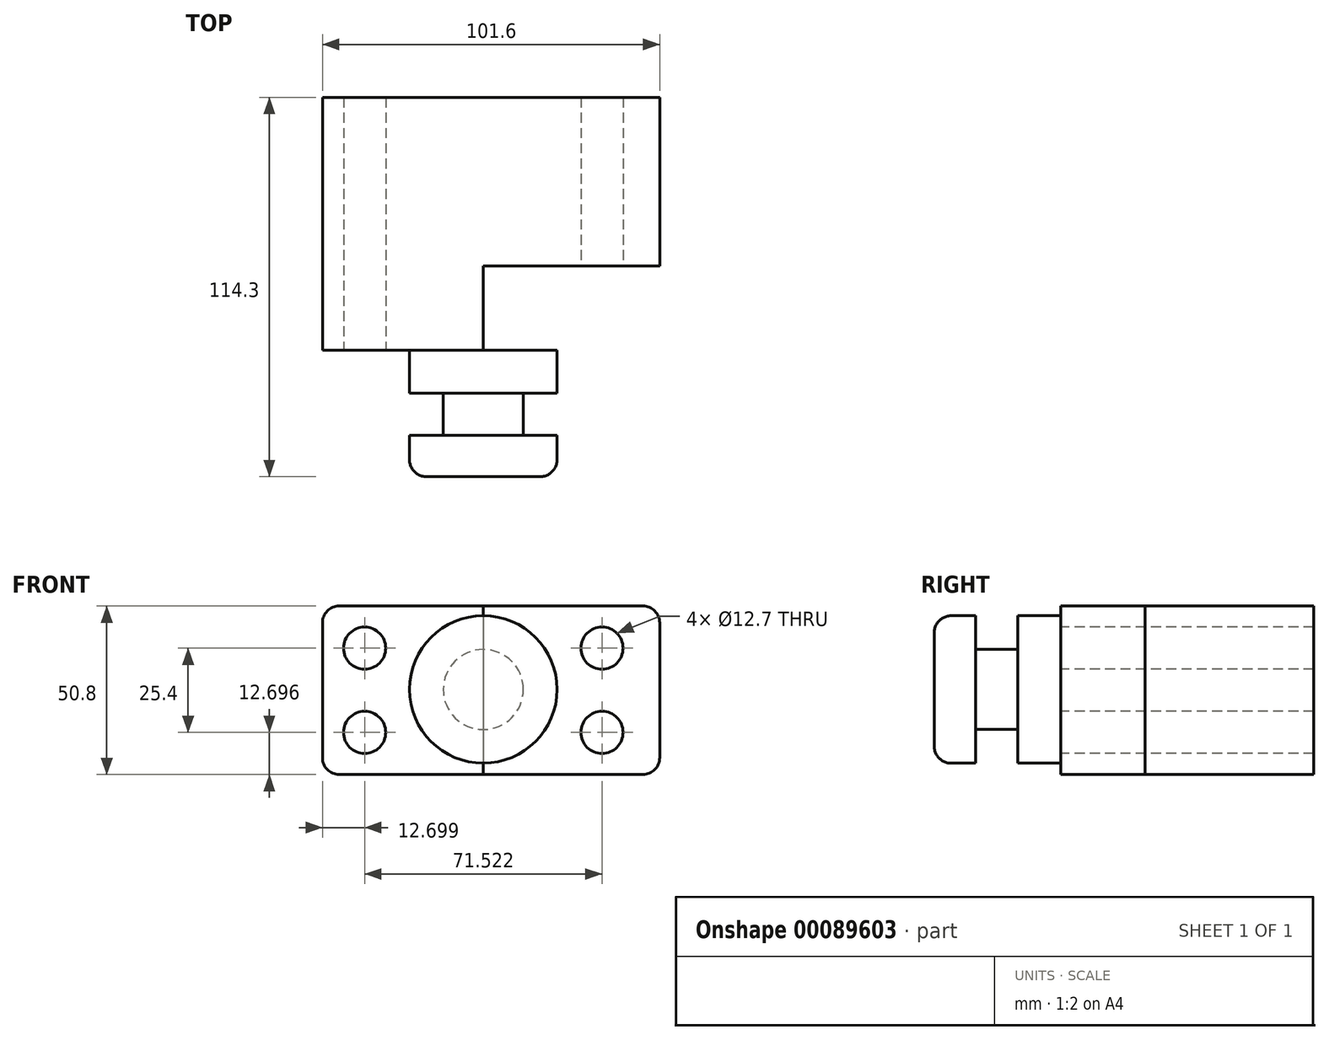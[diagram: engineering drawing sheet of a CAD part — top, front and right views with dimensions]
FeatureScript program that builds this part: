
annotation { "Feature Type Name" : "Feature", "Feature Type Description" : "" }
export const myFeature = defineFeature(function(context is Context, id is Id, definition is map)
    precondition{}
    {
        {
            var Q0;
            Q0=qCreatedBy(makeId("Front.planeOp"),FACE);
            var sketch = newSketch(context, id + "F0", { "sketchPlane" : qUnion([Q0])});
            skLineSegment(sketch, "E0", {"start": v(-48.46, 25.17) * mm, "end": v(53.14, 25.17) * mm});
            skLineSegment(sketch, "E1", {"start": v(53.14, 25.17) * mm, "end": v(53.14, -25.63) * mm});
            skLineSegment(sketch, "E2", {"start": v(53.14, -25.63) * mm, "end": v(-48.46, -25.63) * mm});
            skLineSegment(sketch, "E3", {"start": v(-48.46, -25.63) * mm, "end": v(-48.46, 25.17) * mm});
            skSolve(sketch);
        }
        {
            var Q0;
            Q0=makeQuery(id+"F0.imprint","IMPRINT",FACE,{"disambiguationData":[TD([[makeQuery(id+"F0.imprint","IMPRINT",EDGE,{"derivedFrom":sQuery(id+"F0.wireOp",EDGE,"E0")}),-1.0]])]});
            extrude(context, id + "F1", {"entities" : qUnion([Q0]), "depth" : 76.2 * mm});
        }
        {
            var Q0;
            Q0=makeQuery(id+"F1.opExtrude","CAP_FACE",FACE,{"disambiguationData":[OSD([sQuery(id+"F0.wireOp",EDGE,"E0"),sQuery(id+"F0.wireOp",EDGE,"E1"),sQuery(id+"F0.wireOp",EDGE,"E2"),sQuery(id+"F0.wireOp",EDGE,"E3")])],"isStart":false});
            var sketch = newSketch(context, id + "F2", { "sketchPlane" : qUnion([Q0])});
            skCircle(sketch, "E4", {"center": v(-35.76, 12.47) * mm, "radius": 6.35 * mm});
            skCircle(sketch, "E5", {"center": v(-35.76, -12.93) * mm, "radius": 6.35 * mm});
            skLineSegment(sketch, "E6", {"start": v(0, 32.51) * mm, "end": v(0, -31.69) * mm});
            skCircle(sketch, "E7.MirrorC", {"center": v(35.76, 12.47) * mm, "radius": 6.35 * mm});
            skCircle(sketch, "E8.MirrorC", {"center": v(35.76, -12.93) * mm, "radius": 6.35 * mm});
            skSolve(sketch);
        }
        {
            var Q0;
            Q0=makeQuery(id+"F2.imprint","IMPRINT",FACE,{"disambiguationData":[TD([[makeQuery(id+"F2.imprint","IMPRINT",EDGE,{"derivedFrom":sQuery(id+"F2.wireOp",EDGE,"E7.MirrorC")}),-1.0]])]});
            extrude(context, id + "F3", {"entities" : qUnion([Q0]), "operationType" : NewBodyOperationType.REMOVE, "oppositeDirection" : true, "depth" : 25.4 * mm});
        }
        {
            var Q0;
            Q0 = qSketchRegion(id + "F2", true);
            extrude(context, id + "F4", {"entities" : qUnion([Q0]), "operationType" : NewBodyOperationType.REMOVE, "endBound" : BoundingType.THROUGH_ALL, "oppositeDirection" : true, "depth" : 25.4 * mm});
        }
        {
            var Q0;
            Q0=qCreatedBy(makeId("Right.planeOp"),FACE);
            var sketch = newSketch(context, id + "F5", { "sketchPlane" : qUnion([Q0])});
            skLineSegment(sketch, "E9.bottom", {"start": v(-76.2, 0) * mm, "end": v(-114.3, 0) * mm});
            skLineSegment(sketch, "E9.top", {"start": v(-76.2, -22.22) * mm, "end": v(-114.3, -22.22) * mm});
            skLineSegment(sketch, "E9.left", {"start": v(-76.2, 0) * mm, "end": v(-76.2, -22.22) * mm});
            skLineSegment(sketch, "E9.right", {"start": v(-114.3, 0) * mm, "end": v(-114.3, -22.22) * mm});
            skSolve(sketch);
        }
        {
            var Q0;
            Q0 = qSketchRegion(id + "F5", true);
            var Q1;
            Q1=sQuery(id+"F5.wireOp",EDGE,"E9.bottom");
            revolve(context, id + "F6", {"entities" : qUnion([Q0]), "axis" : qUnion([Q1]), "revolveType" : RevolveType.FULL});
        }
        {
            var Q0;
            Q0=qCreatedBy(makeId("Top.planeOp"),FACE);
            var sketch = newSketch(context, id + "F7", { "sketchPlane" : qUnion([Q0])});
            skLineSegment(sketch, "E10", {"start": v(0, 0) * mm, "end": v(0, -140.97) * mm, "construction": true});
            skLineSegment(sketch, "E11", {"start": v(22.22, -89.2) * mm, "end": v(22.22, -101.9) * mm});
            skLineSegment(sketch, "E12", {"start": v(22.22, -101.9) * mm, "end": v(12.06, -101.9) * mm});
            skLineSegment(sketch, "E13", {"start": v(12.06, -101.9) * mm, "end": v(12.06, -89.2) * mm});
            skLineSegment(sketch, "E14", {"start": v(12.06, -89.2) * mm, "end": v(22.22, -89.2) * mm});
            skSolve(sketch);
        }
        {
            var Q0;
            Q0 = qSketchRegion(id + "F7", true);
            var Q1;
            Q1=sQuery(id+"F7.wireOp",EDGE,"E10");
            revolve(context, id + "F8", {"operationType" : NewBodyOperationType.REMOVE, "entities" : qUnion([Q0]), "axis" : qUnion([Q1]), "revolveType" : RevolveType.FULL, "oppositeDirection" : true});
        }
        {
            var Q0;
            Q0=makeQuery(id+"F6.opRevolve","SWEPT_EDGE",EDGE,{"disambiguationData":[OSD([sQuery(id+"F5.wireOp",EDGE,"E9.top"),sQuery(id+"F5.wireOp",EDGE,"E9.right")])]});
            fillet(context, id + "F9", {"entities" : qUnion([Q0]), "radius" : 5.08 * mm, "tangentPropagation" : true, "allowEdgeOverflow" : false});
        }
        {
            var Q0;
            Q0=makeQuery(id+"F1.opExtrude","SWEPT_EDGE",EDGE,{"disambiguationData":[OSD([sQuery(id+"F0.wireOp",EDGE,"E2"),sQuery(id+"F0.wireOp",EDGE,"E3")])]});
            var Q1;
            Q1=makeQuery(id+"F1.opExtrude","SWEPT_EDGE",EDGE,{"disambiguationData":[OSD([sQuery(id+"F0.wireOp",EDGE,"E1"),sQuery(id+"F0.wireOp",EDGE,"E2")])]});
            var Q2;
            Q2=makeQuery(id+"F1.opExtrude","SWEPT_EDGE",EDGE,{"disambiguationData":[OSD([sQuery(id+"F0.wireOp",EDGE,"E0"),sQuery(id+"F0.wireOp",EDGE,"E3")])]});
            fillet(context, id + "F10", {"entities" : qUnion([Q0, Q1, Q2]), "radius" : 5.08 * mm, "tangentPropagation" : true, "allowEdgeOverflow" : false});
        }
        {
            var Q0;
            Q0=makeQuery(id+"F1.opExtrude","SWEPT_EDGE",EDGE,{"disambiguationData":[OSD([sQuery(id+"F0.wireOp",EDGE,"E0"),sQuery(id+"F0.wireOp",EDGE,"E1")])]});
            fillet(context, id + "F11", {"entities" : qUnion([Q0]), "radius" : 5.08 * mm, "tangentPropagation" : true, "allowEdgeOverflow" : false});
        }
    });
